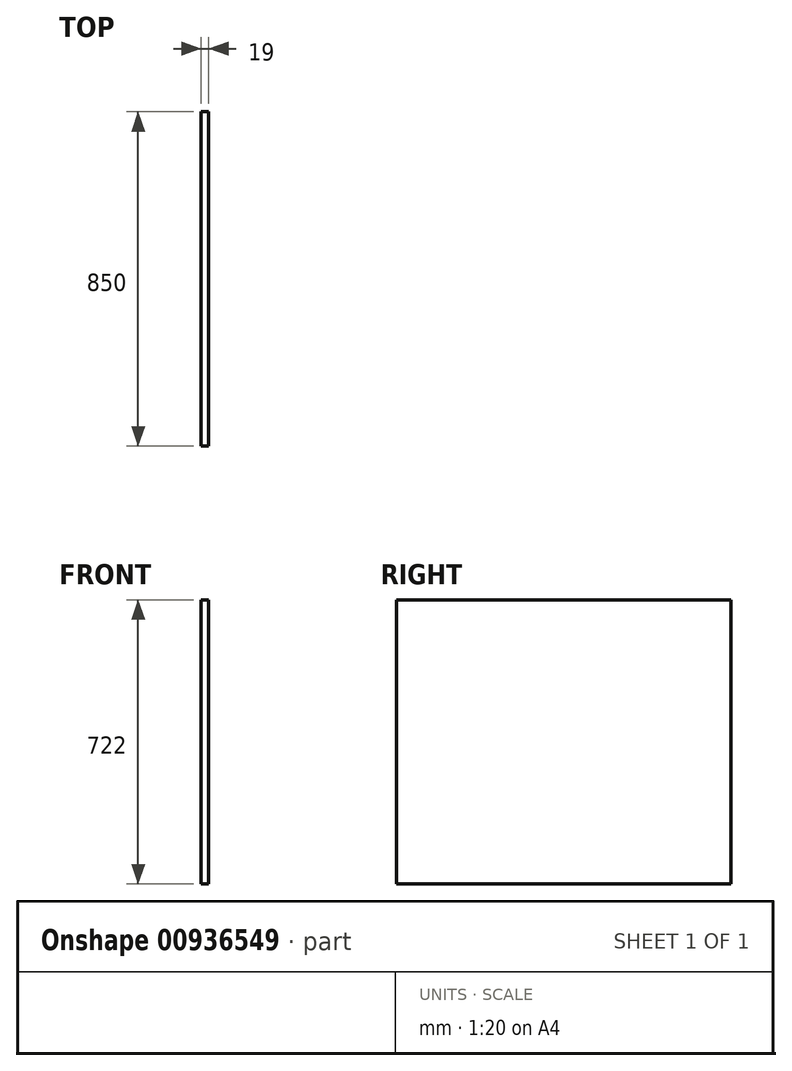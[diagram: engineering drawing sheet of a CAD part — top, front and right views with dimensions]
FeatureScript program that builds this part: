
annotation { "Feature Type Name" : "Feature", "Feature Type Description" : "" }
export const myFeature = defineFeature(function(context is Context, id is Id, definition is map)
    precondition{}
    {
        {
            var Q0;
            Q0=qCreatedBy(makeId("Front.planeOp"),FACE);
            var sketch = newSketch(context, id + "F0", { "sketchPlane" : qUnion([Q0])});
            skLineSegment(sketch, "E0.bottom", {"start": v(9.5, 361) * mm, "end": v(-9.5, 361) * mm});
            skLineSegment(sketch, "E0.top", {"start": v(9.5, -361) * mm, "end": v(-9.5, -361) * mm});
            skLineSegment(sketch, "E0.left", {"start": v(9.5, 361) * mm, "end": v(9.5, -361) * mm});
            skLineSegment(sketch, "E0.right", {"start": v(-9.5, 361) * mm, "end": v(-9.5, -361) * mm});
            skPoint(sketch, "E0.middle", {"position": v(0, 0) * mm});
            skSolve(sketch);
        }
        {
            var Q0;
            Q0=makeQuery(id+"F0.imprint","IMPRINT",FACE,{"disambiguationData":[TD([[makeQuery(id+"F0.imprint","IMPRINT",EDGE,{"derivedFrom":sQuery(id+"F0.wireOp",EDGE,"E0.bottom")}),1.0]])]});
            extrude(context, id + "F1", {"entities" : qUnion([Q0]), "depth" : 850 * mm, "offsetDistance" : 25 * mm});
        }
    });
